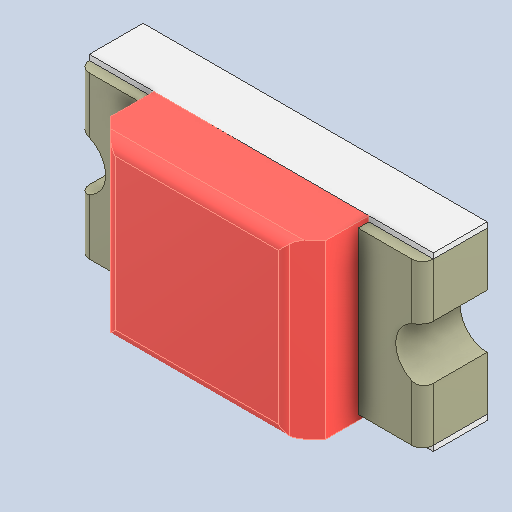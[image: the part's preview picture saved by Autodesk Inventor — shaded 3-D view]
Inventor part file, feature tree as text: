
AUTODESK INVENTOR PART (.ipt)
format: ipt  version: 2022 (Build 260153000, 153)  size: 160,768 bytes
history: native  units: in
note: dims shown in document units (in); Inventor stores cm internally (conversion verified against a paired STEP export)
features: fillet x2, other x2
ambient origin geometry x8: Origin, YZ Plane, XZ Plane, XY Plane, X Axis, Y Axis, Z Axis, Center Point
bodies: Solid1 (feature_tree), Solid2 (feature_tree), Solid3 (feature_tree), Solid4 (feature_tree)
feature tree (4):
  fillet  "Fillet001_(Solid)001:1"  [1 undecoded]
  fillet  "Fillet001_(Solid):1"  [1 undecoded]
  other  "Lens:1"
  other  "Base:1"
note: 2 required parameter values undecoded (feature->parameter linkage not recoverable at this tier; creation-order binding heuristic only, values carry confidence <= 0.55)
